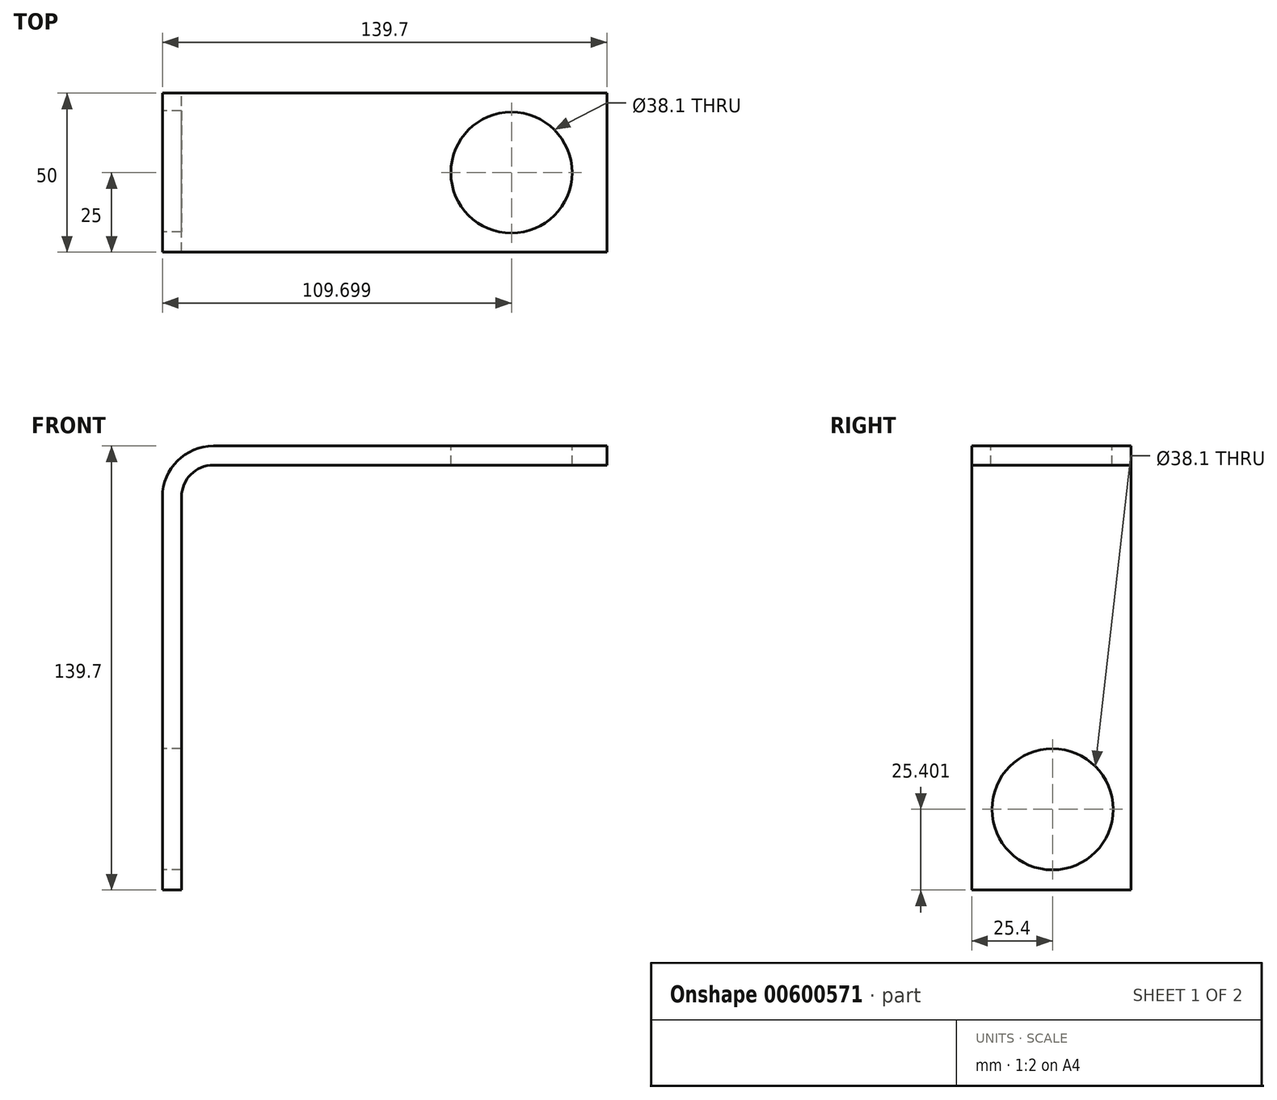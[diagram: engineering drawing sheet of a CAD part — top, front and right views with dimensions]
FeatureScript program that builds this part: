
annotation { "Feature Type Name" : "Feature", "Feature Type Description" : "" }
export const myFeature = defineFeature(function(context is Context, id is Id, definition is map)
    precondition{}
    {
        {
            var Q0;
            Q0=qCreatedBy(makeId("Front.planeOp"),FACE);
            var sketch = newSketch(context, id + "F0", { "sketchPlane" : qUnion([Q0])});
            skLineSegment(sketch, "E0", {"start": v(-53.07, -101.29) * mm, "end": v(-53.07, 22.41) * mm});
            skLineSegment(sketch, "E1", {"start": v(-37.07, 38.41) * mm, "end": v(86.63, 38.41) * mm});
            skLineSegment(sketch, "E2", {"start": v(86.63, 38.41) * mm, "end": v(86.63, 32.41) * mm});
            skLineSegment(sketch, "E3", {"start": v(-53.07, -101.29) * mm, "end": v(-47.07, -101.29) * mm});
            skPoint(sketch, "E4.visualSharp", {"position": v(-53.07, 38.41) * mm});
            skArc(sketch, "E4.filletArc", {"start": v(-37.07, 38.41) * mm, "mid": v(-48.38, 33.72) * mm, "end": v(-53.07, 22.41) * mm});
            skLineSegment(sketch, "E5", {"start": v(-47.07, -101.29) * mm, "end": v(-47.07, 22.41) * mm});
            skLineSegment(sketch, "E6", {"start": v(86.63, 32.41) * mm, "end": v(-37.07, 32.41) * mm});
            skPoint(sketch, "E7.newPointB", {"position": v(-47.07, 22.41) * mm});
            skArc(sketch, "E7.filletArc", {"start": v(-37.07, 32.41) * mm, "mid": v(-44.14, 29.48) * mm, "end": v(-47.07, 22.41) * mm});
            skSolve(sketch);
        }
        {
            var Q0;
            Q0=makeQuery(id+"F0.imprint","IMPRINT",FACE,{"disambiguationData":[TD([[makeQuery(id+"F0.imprint","IMPRINT",EDGE,{"derivedFrom":sQuery(id+"F0.wireOp",EDGE,"E0")}),-1.0]])]});
            extrude(context, id + "F1", {"entities" : qUnion([Q0]), "depth" : 50 * mm});
        }
        {
            var Q0;
            Q0=makeQuery(id+"F1.opExtrude","SWEPT_FACE",FACE,{"disambiguationData":[OSD([sQuery(id+"F0.wireOp",EDGE,"E1")])]});
            var sketch = newSketch(context, id + "F2", { "sketchPlane" : qUnion([Q0])});
            skLineSegment(sketch, "E8", {"start": v(86.63, -25) * mm, "end": v(-37.07, -25) * mm, "construction": true});
            skLineSegment(sketch, "E9", {"start": v(86.63, -25) * mm, "end": v(56.63, -25) * mm, "construction": true});
            skLineSegment(sketch, "E10", {"start": v(56.63, -25) * mm, "end": v(-3.37, -25) * mm, "construction": true});
            skCircle(sketch, "E11", {"center": v(56.63, -25) * mm, "radius": 19.05 * mm});
            skSolve(sketch);
        }
        {
            var Q0;
            Q0=qSketchRegion(id+"F2",true);
            extrude(context, id + "F3", {"entities" : qUnion([Q0]), "operationType" : NewBodyOperationType.REMOVE, "oppositeDirection" : true, "depth" : 25 * mm});
        }
        {
            var Q0;
            Q0=makeQuery(id+"F1.opExtrude","SWEPT_FACE",FACE,{"disambiguationData":[OSD([sQuery(id+"F0.wireOp",EDGE,"E0")])]});
            var sketch = newSketch(context, id + "F4", { "sketchPlane" : qUnion([Q0])});
            skLineSegment(sketch, "E12", {"start": v(25, -101.29) * mm, "end": v(25, -25.46) * mm, "construction": true});
            skLineSegment(sketch, "E13", {"start": v(25, -101.29) * mm, "end": v(25, -85.98) * mm, "construction": true});
            skLineSegment(sketch, "E14", {"start": v(19.46, -66.29) * mm, "end": v(7.4, -66.29) * mm, "construction": true});
            skLineSegment(sketch, "E15", {"start": v(6.56, -75.89) * mm, "end": v(30.2, -75.89) * mm, "construction": true});
            skLineSegment(sketch, "E16", {"start": v(24.6, -69.87) * mm, "end": v(24.6, -80.55) * mm, "construction": true});
            skPoint(sketch, "E17", {"position": v(12.5, -66.29) * mm});
            skPoint(sketch, "E17.positionSnap0", {"position": v(13.43, -66.29) * mm});
            skPoint(sketch, "E18", {"position": v(24.6, -75.89) * mm});
            skCircle(sketch, "E19", {"center": v(24.6, -75.89) * mm, "radius": 19.05 * mm});
            skSolve(sketch);
        }
        {
            var Q0;
            Q0=qSketchRegion(id+"F4",true);
            extrude(context, id + "F5", {"entities" : qUnion([Q0]), "operationType" : NewBodyOperationType.REMOVE, "oppositeDirection" : true, "depth" : 25 * mm});
        }
    });
